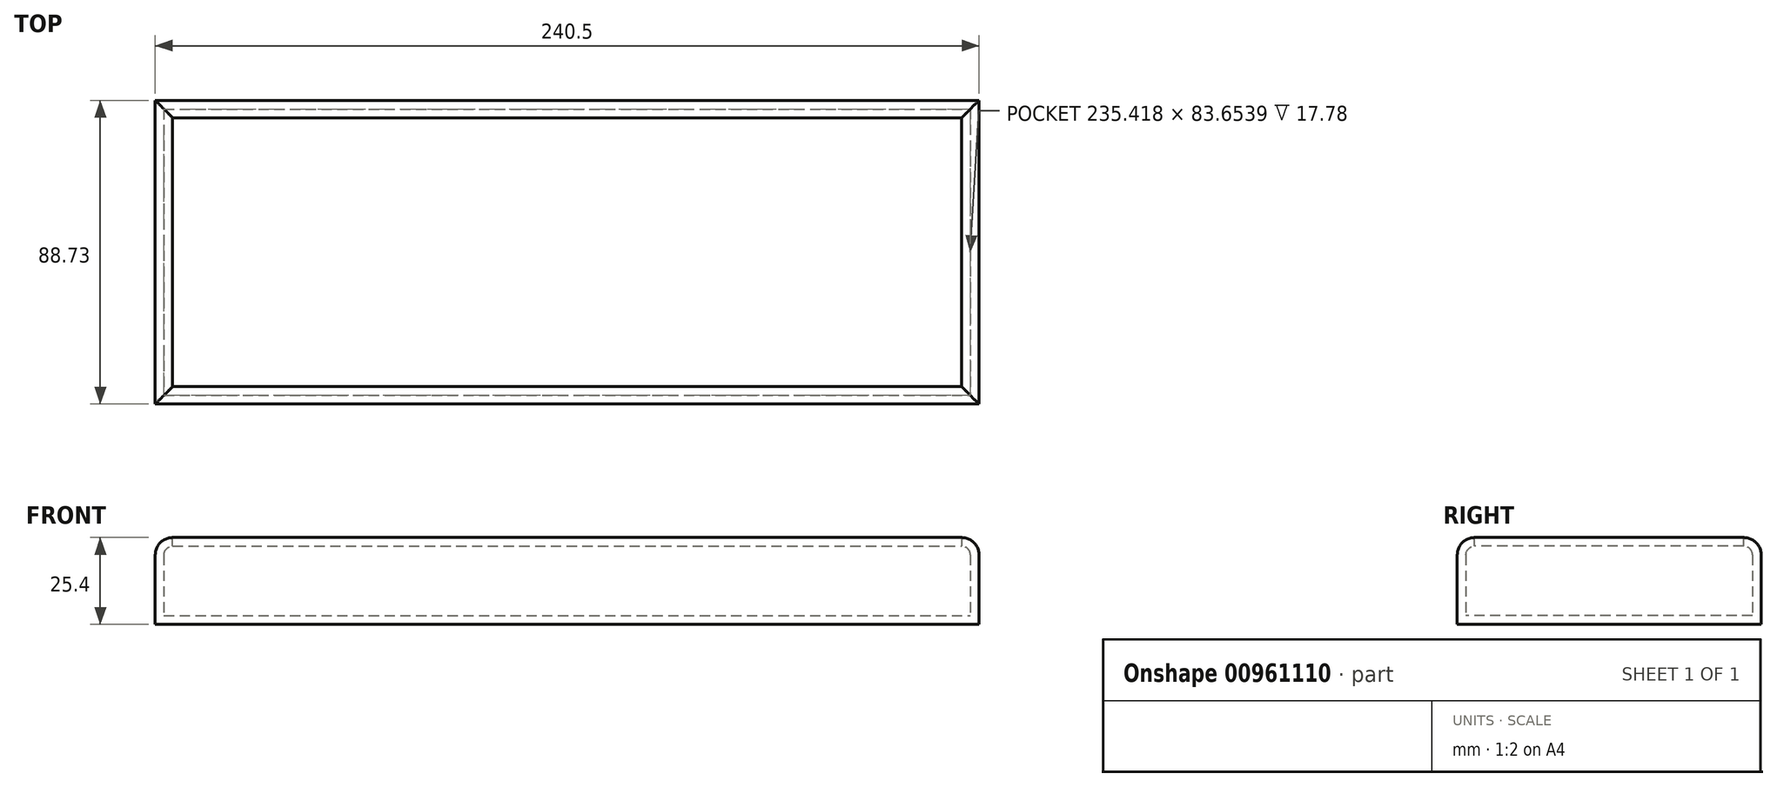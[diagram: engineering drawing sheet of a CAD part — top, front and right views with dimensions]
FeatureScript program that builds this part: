
annotation { "Feature Type Name" : "Feature", "Feature Type Description" : "" }
export const myFeature = defineFeature(function(context is Context, id is Id, definition is map)
    precondition{}
    {
        {
            var Q0;
            Q0=qCreatedBy(makeId("Top.planeOp"),FACE);
            var sketch = newSketch(context, id + "F0", { "sketchPlane" : qUnion([Q0])});
            skLineSegment(sketch, "E0.bottom", {"start": v(-124.29, 47.84) * mm, "end": v(116.21, 47.84) * mm});
            skLineSegment(sketch, "E0.top", {"start": v(-124.29, -40.9) * mm, "end": v(116.21, -40.9) * mm});
            skLineSegment(sketch, "E0.left", {"start": v(-124.29, 47.84) * mm, "end": v(-124.29, -40.9) * mm});
            skLineSegment(sketch, "E0.right", {"start": v(116.21, 47.84) * mm, "end": v(116.21, -40.9) * mm});
            skSolve(sketch);
        }
        {
            var Q0;
            Q0=makeQuery(id+"F0.imprint","IMPRINT",FACE,{"disambiguationData":[TD([[makeQuery(id+"F0.imprint","IMPRINT",EDGE,{"derivedFrom":sQuery(id+"F0.wireOp",EDGE,"E0.bottom")}),-1.0]])]});
            extrude(context, id + "F1", {"entities" : qUnion([Q0]), "depth" : 25.4 * mm, "offsetDistance" : 25.4 * mm});
        }
        {
            var Q0;
            Q0=makeQuery(id+"F1.opExtrude","CAP_FACE",FACE,{"disambiguationData":[OSD([sQuery(id+"F0.wireOp",EDGE,"E0.bottom"),sQuery(id+"F0.wireOp",EDGE,"E0.top"),sQuery(id+"F0.wireOp",EDGE,"E0.left"),sQuery(id+"F0.wireOp",EDGE,"E0.right")])],"isStart":false});
            fillet(context, id + "F2", {"entities" : qUnion([Q0]), "radius" : 5.08 * mm, "tangentPropagation" : true, "allowEdgeOverflow" : false});
        }
        {
            var Q0;
            Q0=makeQuery(id+"F1.opExtrude","CAP_FACE",FACE,{"disambiguationData":[OSD([sQuery(id+"F0.wireOp",EDGE,"E0.bottom"),sQuery(id+"F0.wireOp",EDGE,"E0.top"),sQuery(id+"F0.wireOp",EDGE,"E0.left"),sQuery(id+"F0.wireOp",EDGE,"E0.right")])],"isStart":false});
            shell(context, id + "F3", {"entities" : qUnion([Q0]), "thickness" : 2.54 * mm});
        }
    });
